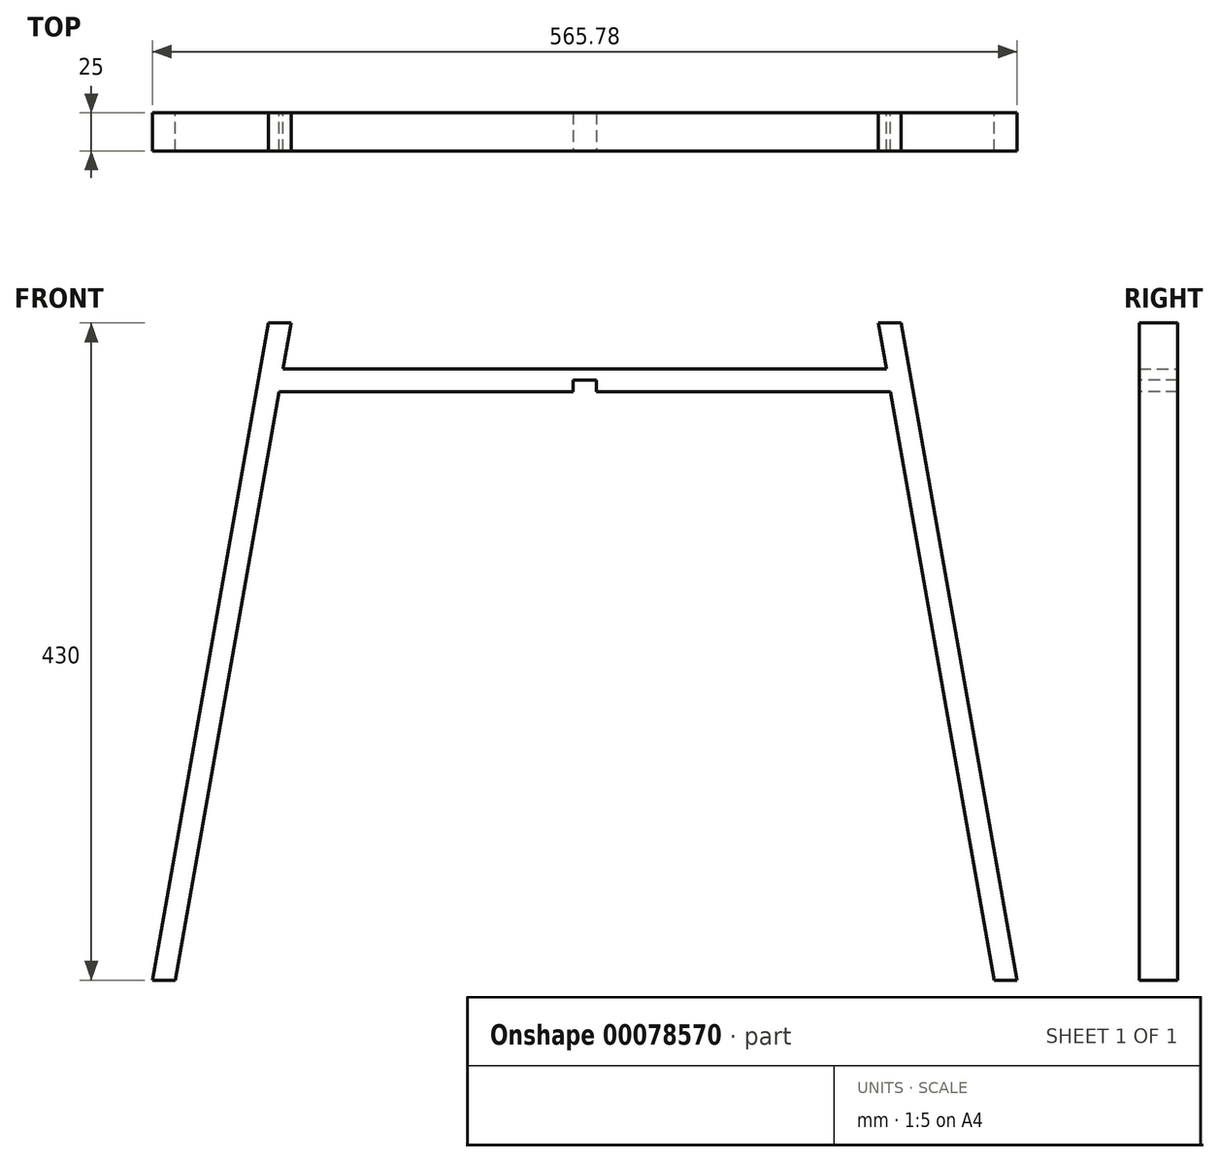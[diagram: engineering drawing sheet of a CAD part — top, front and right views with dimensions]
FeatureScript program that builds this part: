
annotation { "Feature Type Name" : "Feature", "Feature Type Description" : "" }
export const myFeature = defineFeature(function(context is Context, id is Id, definition is map)
    precondition{}
    {
        {
            var Q0;
            Q0=qCreatedBy(makeId("Front.planeOp"),FACE);
            var sketch = newSketch(context, id + "F0", { "sketchPlane" : qUnion([Q0])});
            skLineSegment(sketch, "E0", {"start": v(-282.89, 0) * mm, "end": v(-207.07, 430) * mm});
            skLineSegment(sketch, "E1", {"start": v(-207.07, 430) * mm, "end": v(-192.07, 430) * mm});
            skLineSegment(sketch, "E2", {"start": v(-192.07, 430) * mm, "end": v(-197.36, 400) * mm});
            skLineSegment(sketch, "E3", {"start": v(-197.36, 400) * mm, "end": v(0, 400) * mm});
            skLineSegment(sketch, "E4", {"start": v(0, 400) * mm, "end": v(0, 385) * mm});
            skLineSegment(sketch, "E5", {"start": v(0, 385) * mm, "end": v(-200, 385) * mm});
            skLineSegment(sketch, "E6", {"start": v(-200, 385) * mm, "end": v(-267.89, 0) * mm});
            skLineSegment(sketch, "E7", {"start": v(-267.89, 0) * mm, "end": v(-282.89, 0) * mm});
            skLineSegment(sketch, "E8.MirrorCS", {"start": v(267.89, 0) * mm, "end": v(282.89, 0) * mm});
            skLineSegment(sketch, "E9.MirrorCS", {"start": v(207.07, 430) * mm, "end": v(192.07, 430) * mm});
            skLineSegment(sketch, "E10.MirrorCS", {"start": v(0, 385) * mm, "end": v(200, 385) * mm});
            skLineSegment(sketch, "E11.MirrorCS", {"start": v(200, 385) * mm, "end": v(267.89, 0) * mm});
            skLineSegment(sketch, "E12.MirrorCS", {"start": v(192.07, 430) * mm, "end": v(197.36, 400) * mm});
            skLineSegment(sketch, "E13.MirrorCS", {"start": v(197.36, 400) * mm, "end": v(0, 400) * mm});
            skLineSegment(sketch, "E14.MirrorCS", {"start": v(282.89, 0) * mm, "end": v(207.07, 430) * mm});
            skSolve(sketch);
        }
        {
            var Q0;
            Q0=makeQuery(id+"F0.imprint","IMPRINT",FACE,{"disambiguationData":[TD([[makeQuery(id+"F0.imprint","IMPRINT",EDGE,{"derivedFrom":sQuery(id+"F0.wireOp",EDGE,"E8.MirrorCS")}),1.0]])]});
            var Q1;
            Q1=makeQuery(id+"F0.imprint","IMPRINT",FACE,{"disambiguationData":[TD([[makeQuery(id+"F0.imprint","IMPRINT",EDGE,{"derivedFrom":sQuery(id+"F0.wireOp",EDGE,"E0")}),-1.0]])]});
            extrude(context, id + "F1", {"entities" : qUnion([Q0, Q1]), "depth" : 25 * mm});
        }
        {
            var Q0;
            Q0=makeQuery(id+"F1.opExtrude","CAP_FACE",FACE,{"disambiguationData":[OSD([sQuery(id+"F0.wireOp",EDGE,"E0"),sQuery(id+"F0.wireOp",EDGE,"E1"),sQuery(id+"F0.wireOp",EDGE,"E2"),sQuery(id+"F0.wireOp",EDGE,"E3"),sQuery(id+"F0.wireOp",EDGE,"E5"),sQuery(id+"F0.wireOp",EDGE,"E6"),sQuery(id+"F0.wireOp",EDGE,"E7"),sQuery(id+"F0.wireOp",EDGE,"E8.MirrorCS"),sQuery(id+"F0.wireOp",EDGE,"E9.MirrorCS"),sQuery(id+"F0.wireOp",EDGE,"E10.MirrorCS"),sQuery(id+"F0.wireOp",EDGE,"E11.MirrorCS"),sQuery(id+"F0.wireOp",EDGE,"E12.MirrorCS"),sQuery(id+"F0.wireOp",EDGE,"E13.MirrorCS"),sQuery(id+"F0.wireOp",EDGE,"E14.MirrorCS")])],"isStart":false});
            var sketch = newSketch(context, id + "F2", { "sketchPlane" : qUnion([Q0])});
            skLineSegment(sketch, "E15.bottom", {"start": v(-7.5, 385) * mm, "end": v(7.5, 385) * mm});
            skLineSegment(sketch, "E15.top", {"start": v(-7.5, 392.5) * mm, "end": v(7.5, 392.5) * mm});
            skLineSegment(sketch, "E15.left", {"start": v(-7.5, 385) * mm, "end": v(-7.5, 392.5) * mm});
            skLineSegment(sketch, "E15.right", {"start": v(7.5, 385) * mm, "end": v(7.5, 392.5) * mm});
            skSolve(sketch);
        }
        {
            var Q0;
            Q0 = qSketchRegion(id + "F2", true);
            extrude(context, id + "F3", {"entities" : qUnion([Q0]), "operationType" : NewBodyOperationType.REMOVE, "endBound" : BoundingType.UP_TO_NEXT, "oppositeDirection" : true, "depth" : 25 * mm});
        }
    });
